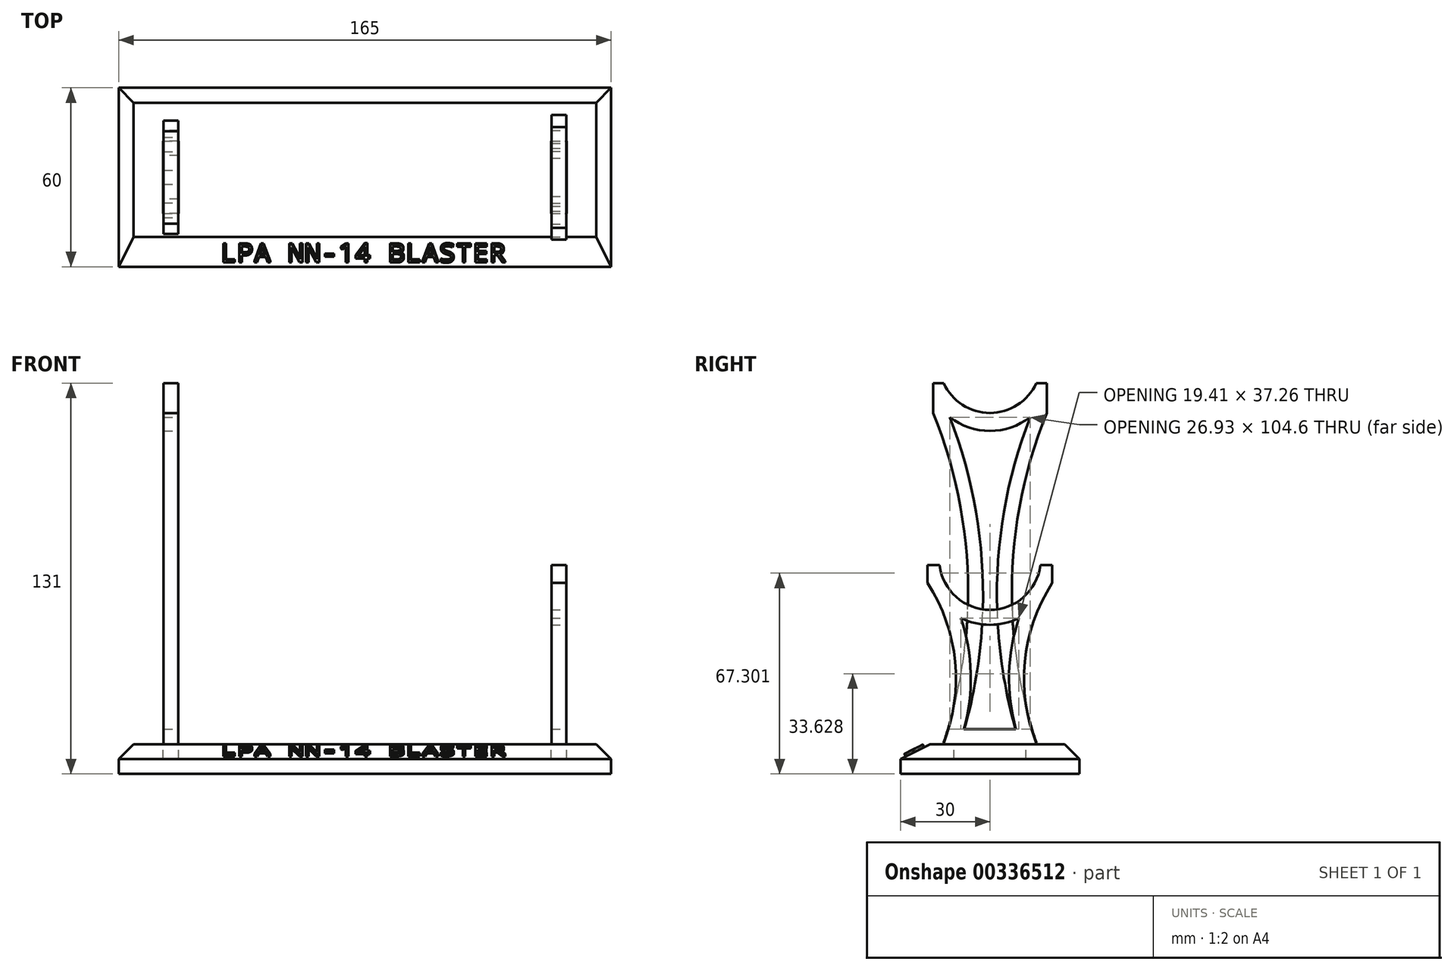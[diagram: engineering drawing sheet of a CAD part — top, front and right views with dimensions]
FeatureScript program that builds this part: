
annotation { "Feature Type Name" : "Feature", "Feature Type Description" : "" }
export const myFeature = defineFeature(function(context is Context, id is Id, definition is map)
    precondition{}
    {
        {
            var Q0;
            Q0=qCreatedBy(makeId("Right.planeOp"),FACE);
            cPlane(context, id + "F0", {"entities" : qUnion([Q0]), "cplaneType" : CPlaneType.OFFSET, "offset" : 50 * mm, "oppositeDirection" : true, "width" : 150 * mm, "height" : 150 * mm});
        }
        {
            var Q0;
            Q0=qCreatedBy(id+"F0.planeOp",FACE);
            var sketch = newSketch(context, id + "F1", { "sketchPlane" : qUnion([Q0])});
            skLineSegment(sketch, "E0", {"start": v(0, 0) * mm, "end": v(0, 120) * mm, "construction": true});
            skLineSegment(sketch, "E1", {"start": v(0, 120) * mm, "end": v(0, 128) * mm});
            skArc(sketch, "E2", {"start": v(-15.5, 121) * mm, "mid": v(0, 111) * mm, "end": v(15.5, 121) * mm});
            skLineSegment(sketch, "E3", {"start": v(19, 111) * mm, "end": v(19, 121) * mm});
            skLineSegment(sketch, "E4", {"start": v(19, 121) * mm, "end": v(15.5, 121) * mm});
            skLineSegment(sketch, "E5", {"start": v(-19, 121) * mm, "end": v(-19, 111) * mm});
            skLineSegment(sketch, "E6.trimOffspring", {"start": v(-15.5, 121) * mm, "end": v(-19, 121) * mm});
            skLineSegment(sketch, "E7", {"start": v(-15.67, 0) * mm, "end": v(-12, 0) * mm});
            skLineSegment(sketch, "E8", {"start": v(0, 0) * mm, "end": v(0, -5) * mm});
            skLineSegment(sketch, "E9", {"start": v(-12, -5) * mm, "end": v(12, -5) * mm});
            skLineSegment(sketch, "E10", {"start": v(12, -5) * mm, "end": v(12, 0) * mm});
            skLineSegment(sketch, "E11.MirrorCS", {"start": v(-12, -5) * mm, "end": v(-12, 0) * mm});
            skArc(sketch, "E12", {"start": v(19, 111) * mm, "mid": v(7.4, 55.8) * mm, "end": v(15.67, 0) * mm});
            skArc(sketch, "E13", {"start": v(-15.67, 0) * mm, "mid": v(-7.4, 55.8) * mm, "end": v(-19, 111) * mm});
            skLineSegment(sketch, "E14.trimOffspring", {"start": v(12, 0) * mm, "end": v(15.67, 0) * mm});
            skSolve(sketch);
        }
        {
            var Q0;
            Q0 = qSketchRegion(id + "F1", true);
            extrude(context, id + "F2", {"entities" : qUnion([Q0]), "depth" : 5 * mm});
        }
        {
            var Q0;
            Q0=qCreatedBy(id+"F0.planeOp",FACE);
            cPlane(context, id + "F3", {"entities" : qUnion([Q0]), "cplaneType" : CPlaneType.OFFSET, "offset" : 135 * mm, "width" : 150 * mm, "height" : 150 * mm});
        }
        {
            var Q0;
            Q0=qCreatedBy(id+"F3.planeOp",FACE);
            var sketch = newSketch(context, id + "F4", { "sketchPlane" : qUnion([Q0])});
            skLineSegment(sketch, "E15.0", {"start": v(-15.67, 0) * mm, "end": v(-12, 0) * mm});
            skPoint(sketch, "E16.0", {"position": v(-12, -2.5) * mm});
            skLineSegment(sketch, "E17.0", {"start": v(-12, -5) * mm, "end": v(12, -5) * mm});
            skLineSegment(sketch, "E18.0", {"start": v(12, -5) * mm, "end": v(12, 0) * mm});
            skLineSegment(sketch, "E19.0", {"start": v(12, 0) * mm, "end": v(15.67, 0) * mm});
            skLineSegment(sketch, "E20.0", {"start": v(-12, -5) * mm, "end": v(-12, 0) * mm});
            skLineSegment(sketch, "E21", {"start": v(0, 0) * mm, "end": v(0, 45) * mm});
            skLineSegment(sketch, "E22", {"start": v(0, 45) * mm, "end": v(0, 62) * mm});
            skArc(sketch, "E23", {"start": v(-16.88, 60) * mm, "mid": v(0, 45) * mm, "end": v(16.88, 60) * mm});
            skLineSegment(sketch, "E24", {"start": v(-16.88, 60) * mm, "end": v(-20.88, 60) * mm});
            skLineSegment(sketch, "E25", {"start": v(16.88, 60) * mm, "end": v(20.88, 60) * mm});
            skLineSegment(sketch, "E26", {"start": v(20.88, 60) * mm, "end": v(20.88, 54) * mm});
            skLineSegment(sketch, "E27", {"start": v(-20.88, 60) * mm, "end": v(-20.88, 54) * mm});
            skArc(sketch, "E28", {"start": v(-15.67, 0) * mm, "mid": v(-11.67, 27.64) * mm, "end": v(-20.88, 54) * mm});
            skArc(sketch, "E29.MirrorCS", {"start": v(15.67, 0) * mm, "mid": v(11.67, 27.64) * mm, "end": v(20.88, 54) * mm});
            skSolve(sketch);
        }
        {
            var Q0;
            Q0 = qSketchRegion(id + "F4", true);
            extrude(context, id + "F5", {"entities" : qUnion([Q0]), "oppositeDirection" : true, "depth" : 5 * mm});
        }
        {
            var Q0;
            Q0=qCreatedBy(id+"F3.planeOp",FACE);
            cPlane(context, id + "F6", {"entities" : qUnion([Q0]), "cplaneType" : CPlaneType.OFFSET, "offset" : 15 * mm, "width" : 150 * mm, "height" : 150 * mm});
        }
        {
            var Q0;
            Q0=qCreatedBy(id+"F6.planeOp",FACE);
            var sketch = newSketch(context, id + "F7", { "sketchPlane" : qUnion([Q0])});
            skLineSegment(sketch, "E30", {"start": v(0, 0) * mm, "end": v(-30, 0) * mm});
            skLineSegment(sketch, "E31", {"start": v(0, 0) * mm, "end": v(30, 0) * mm});
            skLineSegment(sketch, "E32", {"start": v(30, 0) * mm, "end": v(30, -10) * mm});
            skLineSegment(sketch, "E33", {"start": v(30, -10) * mm, "end": v(-30, -10) * mm});
            skLineSegment(sketch, "E34", {"start": v(-30, -10) * mm, "end": v(-30, 0) * mm});
            skSolve(sketch);
        }
        {
            var Q0;
            Q0 = qSketchRegion(id + "F7", true);
            extrude(context, id + "F8", {"entities" : qUnion([Q0]), "oppositeDirection" : true, "depth" : 165 * mm});
        }
        {
            var Q0;
            Q0=makeQuery(id+"F8.opExtrude","SWEPT_EDGE",EDGE,{"disambiguationData":[OSD([sQuery(id+"F7.wireOp",EDGE,"E31"),sQuery(id+"F7.wireOp",EDGE,"E32")])]});
            var Q1;
            Q1=makeQuery(id+"F8.opExtrude","CAP_EDGE",EDGE,{"disambiguationData":[OSD([sQuery(id+"F7.wireOp",EDGE,"E30"),sQuery(id+"F7.wireOp",EDGE,"E31")])],"isStart":true});
            var Q2;
            Q2=makeQuery(id+"F8.opExtrude","CAP_EDGE",EDGE,{"disambiguationData":[OSD([sQuery(id+"F7.wireOp",EDGE,"E30"),sQuery(id+"F7.wireOp",EDGE,"E31")])],"isStart":false});
            chamfer(context, id + "F9", {"entities" : qUnion([Q0, Q1, Q2]), "width" : 5 * mm, "tangentPropagation" : true});
        }
        {
            var Q0;
            Q0=makeQuery(id+"F5.opExtrude","SWEPT_BODY",BODY,{"disambiguationData":[OSD([sQuery(id+"F4.wireOp",EDGE,"E15.0"),sQuery(id+"F4.wireOp",EDGE,"E17.0"),sQuery(id+"F4.wireOp",EDGE,"E18.0"),sQuery(id+"F4.wireOp",EDGE,"E19.0"),sQuery(id+"F4.wireOp",EDGE,"E20.0"),sQuery(id+"F4.wireOp",EDGE,"E23"),sQuery(id+"F4.wireOp",EDGE,"Sd1OLZYa-OnP1-l3Yc-naMz-eD3mMwA9oDP4"),sQuery(id+"F4.wireOp",EDGE,"b2450b83-d63d-45a6-ae7f-2fe9c57433fe.0"),sQuery(id+"F4.wireOp",EDGE,"HdVY3prL-ZTQW-y1fw-TBds-aAc6igIkFyQi"),sQuery(id+"F4.wireOp",EDGE,"wTelJ6eU-RCiW-lFgJ-9vya-DIwEEDSqaYIV"),sQuery(id+"F4.wireOp",EDGE,"szUcnAx7-VCeO-wAfL-Jugm-QGzzVLHaK3Rj"),sQuery(id+"F4.wireOp",EDGE,"460e58c3-e8ee-4b37-89e0-f99bfcb21106.trimOffspring")])]});
            transform(context, id + "F10", {"entities" : qUnion([Q0]), "transformType" : TransformType.TRANSLATION_3D, "dx" : 0 * mm, "dy" : 0 * mm, "dz" : 0 * mm, "makeCopy" : true});
        }
        {
            var Q0;
            Q0=makeQuery(id+"F2.opExtrude","SWEPT_BODY",BODY,{"disambiguationData":[OSD([sQuery(id+"F1.wireOp",EDGE,"E2"),sQuery(id+"F1.wireOp",EDGE,"E3"),sQuery(id+"F1.wireOp",EDGE,"E4"),sQuery(id+"F1.wireOp",EDGE,"E5"),sQuery(id+"F1.wireOp",EDGE,"E6.trimOffspring"),sQuery(id+"F1.wireOp",EDGE,"E7"),sQuery(id+"F1.wireOp",EDGE,"E9"),sQuery(id+"F1.wireOp",EDGE,"E10"),sQuery(id+"F1.wireOp",EDGE,"E11.MirrorCS"),sQuery(id+"F1.wireOp",EDGE,"E12"),sQuery(id+"F1.wireOp",EDGE,"E13"),sQuery(id+"F1.wireOp",EDGE,"E14.trimOffspring")])]});
            transform(context, id + "F11", {"entities" : qUnion([Q0]), "transformType" : TransformType.TRANSLATION_3D, "dx" : 0 * mm, "dy" : 0 * mm, "dz" : 0 * mm, "makeCopy" : true});
        }
        {
            var Q0;
            Q0=makeQuery(id+"F2.opExtrude","SWEPT_BODY",BODY,{"disambiguationData":[OSD([sQuery(id+"F1.wireOp",EDGE,"E2"),sQuery(id+"F1.wireOp",EDGE,"E3"),sQuery(id+"F1.wireOp",EDGE,"E4"),sQuery(id+"F1.wireOp",EDGE,"E5"),sQuery(id+"F1.wireOp",EDGE,"E6.trimOffspring"),sQuery(id+"F1.wireOp",EDGE,"E7"),sQuery(id+"F1.wireOp",EDGE,"E9"),sQuery(id+"F1.wireOp",EDGE,"E10"),sQuery(id+"F1.wireOp",EDGE,"E11.MirrorCS"),sQuery(id+"F1.wireOp",EDGE,"E12"),sQuery(id+"F1.wireOp",EDGE,"E13"),sQuery(id+"F1.wireOp",EDGE,"E14.trimOffspring")])]});
            var Q1;
            Q1=makeQuery(id+"F8.opExtrude","SWEPT_BODY",BODY,{"disambiguationData":[OSD([sQuery(id+"F7.wireOp",EDGE,"E30"),sQuery(id+"F7.wireOp",EDGE,"E31"),sQuery(id+"F7.wireOp",EDGE,"E32"),sQuery(id+"F7.wireOp",EDGE,"E33"),sQuery(id+"F7.wireOp",EDGE,"E34")])]});
            booleanBodies(context, id + "F12", {"operationType" : BooleanOperationType.SUBTRACTION, "tools" : qUnion([Q0]), "targets" : qUnion([Q1])});
        }
        {
            var Q0;
            Q0=makeQuery(id+"F5.opExtrude","SWEPT_BODY",BODY,{"disambiguationData":[OSD([sQuery(id+"F4.wireOp",EDGE,"E15.0"),sQuery(id+"F4.wireOp",EDGE,"E17.0"),sQuery(id+"F4.wireOp",EDGE,"E18.0"),sQuery(id+"F4.wireOp",EDGE,"E19.0"),sQuery(id+"F4.wireOp",EDGE,"E20.0"),sQuery(id+"F4.wireOp",EDGE,"E23"),sQuery(id+"F4.wireOp",EDGE,"Sd1OLZYa-OnP1-l3Yc-naMz-eD3mMwA9oDP4"),sQuery(id+"F4.wireOp",EDGE,"b2450b83-d63d-45a6-ae7f-2fe9c57433fe.0"),sQuery(id+"F4.wireOp",EDGE,"HdVY3prL-ZTQW-y1fw-TBds-aAc6igIkFyQi"),sQuery(id+"F4.wireOp",EDGE,"wTelJ6eU-RCiW-lFgJ-9vya-DIwEEDSqaYIV"),sQuery(id+"F4.wireOp",EDGE,"szUcnAx7-VCeO-wAfL-Jugm-QGzzVLHaK3Rj"),sQuery(id+"F4.wireOp",EDGE,"460e58c3-e8ee-4b37-89e0-f99bfcb21106.trimOffspring")])]});
            var Q1;
            Q1=makeQuery(id+"F8.opExtrude","SWEPT_BODY",BODY,{"disambiguationData":[OSD([sQuery(id+"F7.wireOp",EDGE,"E30"),sQuery(id+"F7.wireOp",EDGE,"E31"),sQuery(id+"F7.wireOp",EDGE,"E32"),sQuery(id+"F7.wireOp",EDGE,"E33"),sQuery(id+"F7.wireOp",EDGE,"E34")])]});
            booleanBodies(context, id + "F13", {"operationType" : BooleanOperationType.SUBTRACTION, "tools" : qUnion([Q0]), "targets" : qUnion([Q1])});
        }
        {
            var Q0;
            Q0=makeQuery(id+"F8.opExtrude","SWEPT_FACE",FACE,{"disambiguationData":[OSD([sQuery(id+"F7.wireOp",EDGE,"E30"),sQuery(id+"F7.wireOp",EDGE,"E31")])]});
            var sketch = newSketch(context, id + "F14", { "sketchPlane" : qUnion([Q0])});
            skLineSegment(sketch, "E35.0", {"start": v(-44.9, 12.1) * mm, "end": v(-44.9, -12.1) * mm});
            skLineSegment(sketch, "E36.0", {"start": v(-44.9, 12.1) * mm, "end": v(-50.1, 12.1) * mm});
            skLineSegment(sketch, "E37.0", {"start": v(-50.1, 12.1) * mm, "end": v(-50.1, -12.1) * mm});
            skLineSegment(sketch, "E38.0", {"start": v(-44.9, -12.1) * mm, "end": v(-50.1, -12.1) * mm});
            skSolve(sketch);
        }
        {
            var Q0;
            Q0 = qSketchRegion(id + "F14", true);
            var Q1;
            Q1=makeQuery(id+"F12.opBoolean","COPY",FACE,{"derivedFrom":makeQuery(id+"F2.opExtrude","SWEPT_FACE",FACE,{"disambiguationData":[OSD([sQuery(id+"F1.wireOp",EDGE,"E9")])]})});
            extrude(context, id + "F15", {"entities" : qUnion([Q0]), "operationType" : NewBodyOperationType.REMOVE, "endBound" : BoundingType.UP_TO_SURFACE, "oppositeDirection" : true, "endBoundEntityFace" : qUnion([Q1]), "depth" : 25 * mm});
        }
        {
            var Q0;
            Q0=makeQuery(id+"F8.opExtrude","SWEPT_FACE",FACE,{"disambiguationData":[OSD([sQuery(id+"F7.wireOp",EDGE,"E30"),sQuery(id+"F7.wireOp",EDGE,"E31")])]});
            var sketch = newSketch(context, id + "F16", { "sketchPlane" : qUnion([Q0])});
            skLineSegment(sketch, "E39.0", {"start": v(79.9, 12.1) * mm, "end": v(79.9, -12.1) * mm});
            skLineSegment(sketch, "E40.0", {"start": v(79.9, 12.1) * mm, "end": v(85.1, 12.1) * mm});
            skLineSegment(sketch, "E41.0", {"start": v(85.1, 12.1) * mm, "end": v(85.1, -12.1) * mm});
            skLineSegment(sketch, "E42.0", {"start": v(79.9, -12.1) * mm, "end": v(85.1, -12.1) * mm});
            skSolve(sketch);
        }
        {
            var Q0;
            Q0 = qSketchRegion(id + "F16", true);
            var Q1;
            Q1=makeQuery(id+"F13.opBoolean","COPY",FACE,{"derivedFrom":makeQuery(id+"F5.opExtrude","SWEPT_FACE",FACE,{"disambiguationData":[OSD([sQuery(id+"F4.wireOp",EDGE,"E17.0")])]})});
            extrude(context, id + "F17", {"entities" : qUnion([Q0]), "operationType" : NewBodyOperationType.REMOVE, "endBound" : BoundingType.UP_TO_SURFACE, "oppositeDirection" : true, "endBoundEntityFace" : qUnion([Q1]), "depth" : 25 * mm});
        }
        {
            var Q0;
            Q0=makeQuery(id+"F8.opExtrude","SWEPT_EDGE",EDGE,{"disambiguationData":[OSD([sQuery(id+"F7.wireOp",EDGE,"E30"),sQuery(id+"F7.wireOp",EDGE,"E34")])]});
            chamfer(context, id + "F18", {"entities" : qUnion([Q0]), "chamferType" : ChamferType.TWO_OFFSETS, "width1" : 10 * mm, "oppositeDirection" : false, "width2" : 5 * mm, "tangentPropagation" : true});
        }
        {
            var Q0;
            Q0=makeQuery(id+"F18.opChamfer","BLEND_FACE",FACE,{"disambiguationData":[OSD([sQuery(id+"F7.wireOp",EDGE,"E30"),sQuery(id+"F7.wireOp",EDGE,"E34")])]});
            var sketch = newSketch(context, id + "F19", { "sketchPlane" : qUnion([Q0])});
            skText(sketch, "E43", { "text": "LPA NN-14 BLASTER", "fontName": "DroidSansMono.ttf"});
            const initialGuessF19  = {"E43": [-0.031, -0.02696, 1, 0, 0.00676]};
            skSetInitialGuess(sketch, initialGuessF19);
            skSolve(sketch);
        }
        {
            var Q0;
            Q0 = qSketchRegion(id + "F19", true);
            extrude(context, id + "F20", {"entities" : qUnion([Q0]), "operationType" : NewBodyOperationType.ADD, "depth" : 1 * mm});
        }
        {
            var Q0;
            Q0=makeQuery(id+"F11.opPattern","COPY",FACE,{"derivedFrom":makeQuery(id+"F2.opExtrude","CAP_FACE",FACE,{"disambiguationData":[OSD([sQuery(id+"F1.wireOp",EDGE,"E2"),sQuery(id+"F1.wireOp",EDGE,"E3"),sQuery(id+"F1.wireOp",EDGE,"E4"),sQuery(id+"F1.wireOp",EDGE,"E5"),sQuery(id+"F1.wireOp",EDGE,"E6.trimOffspring"),sQuery(id+"F1.wireOp",EDGE,"E7"),sQuery(id+"F1.wireOp",EDGE,"E9"),sQuery(id+"F1.wireOp",EDGE,"E10"),sQuery(id+"F1.wireOp",EDGE,"E11.MirrorCS"),sQuery(id+"F1.wireOp",EDGE,"E12"),sQuery(id+"F1.wireOp",EDGE,"E13"),sQuery(id+"F1.wireOp",EDGE,"E14.trimOffspring")])],"isStart":false}),"instanceName":"1"});
            var sketch = newSketch(context, id + "F21", { "sketchPlane" : qUnion([Q0])});
            skLineSegment(sketch, "E44.1", {"start": v(-8.58, 5) * mm, "end": v(8.58, 5) * mm});
            skArc(sketch, "E44.3", {"start": v(-13.46, 109.6) * mm, "mid": v(-2.5, 57.7) * mm, "end": v(-8.58, 5) * mm});
            skArc(sketch, "E44.6", {"start": v(8.58, 5) * mm, "mid": v(2.5, 57.7) * mm, "end": v(13.46, 109.6) * mm});
            skArc(sketch, "E44.7", {"start": v(13.46, 109.6) * mm, "mid": v(0, 105) * mm, "end": v(-13.46, 109.6) * mm});
            skSolve(sketch);
        }
        {
            var Q0;
            Q0 = qSketchRegion(id + "F21", true);
            extrude(context, id + "F22", {"entities" : qUnion([Q0]), "operationType" : NewBodyOperationType.REMOVE, "oppositeDirection" : true, "depth" : 25 * mm});
        }
        {
            var Q0;
            Q0=makeQuery(id+"F10.opPattern","COPY",FACE,{"derivedFrom":makeQuery(id+"F5.opExtrude","CAP_FACE",FACE,{"disambiguationData":[OSD([sQuery(id+"F4.wireOp",EDGE,"E15.0"),sQuery(id+"F4.wireOp",EDGE,"E17.0"),sQuery(id+"F4.wireOp",EDGE,"E18.0"),sQuery(id+"F4.wireOp",EDGE,"E19.0"),sQuery(id+"F4.wireOp",EDGE,"E20.0"),sQuery(id+"F4.wireOp",EDGE,"E23"),sQuery(id+"F4.wireOp",EDGE,"Sd1OLZYa-OnP1-l3Yc-naMz-eD3mMwA9oDP4"),sQuery(id+"F4.wireOp",EDGE,"b2450b83-d63d-45a6-ae7f-2fe9c57433fe.0"),sQuery(id+"F4.wireOp",EDGE,"HdVY3prL-ZTQW-y1fw-TBds-aAc6igIkFyQi"),sQuery(id+"F4.wireOp",EDGE,"wTelJ6eU-RCiW-lFgJ-9vya-DIwEEDSqaYIV"),sQuery(id+"F4.wireOp",EDGE,"szUcnAx7-VCeO-wAfL-Jugm-QGzzVLHaK3Rj"),sQuery(id+"F4.wireOp",EDGE,"460e58c3-e8ee-4b37-89e0-f99bfcb21106.trimOffspring")])],"isStart":true}),"instanceName":"1"});
            var sketch = newSketch(context, id + "F23", { "sketchPlane" : qUnion([Q0])});
            skArc(sketch, "E45.0", {"start": v(-8.7, 5) * mm, "mid": v(-6.42, 23.7) * mm, "end": v(-9.7, 42.26) * mm});
            skArc(sketch, "E46.0", {"start": v(8.7, 5) * mm, "mid": v(6.42, 23.7) * mm, "end": v(9.7, 42.26) * mm});
            skLineSegment(sketch, "E47.0", {"start": v(-8.7, 5) * mm, "end": v(8.7, 5) * mm});
            skArc(sketch, "E48.0", {"start": v(-9.7, 42.26) * mm, "mid": v(0, 40) * mm, "end": v(9.7, 42.26) * mm});
            skSolve(sketch);
        }
        {
            var Q0;
            Q0 = qSketchRegion(id + "F23", true);
            extrude(context, id + "F24", {"entities" : qUnion([Q0]), "operationType" : NewBodyOperationType.REMOVE, "oppositeDirection" : true, "depth" : 25 * mm});
        }
    });
